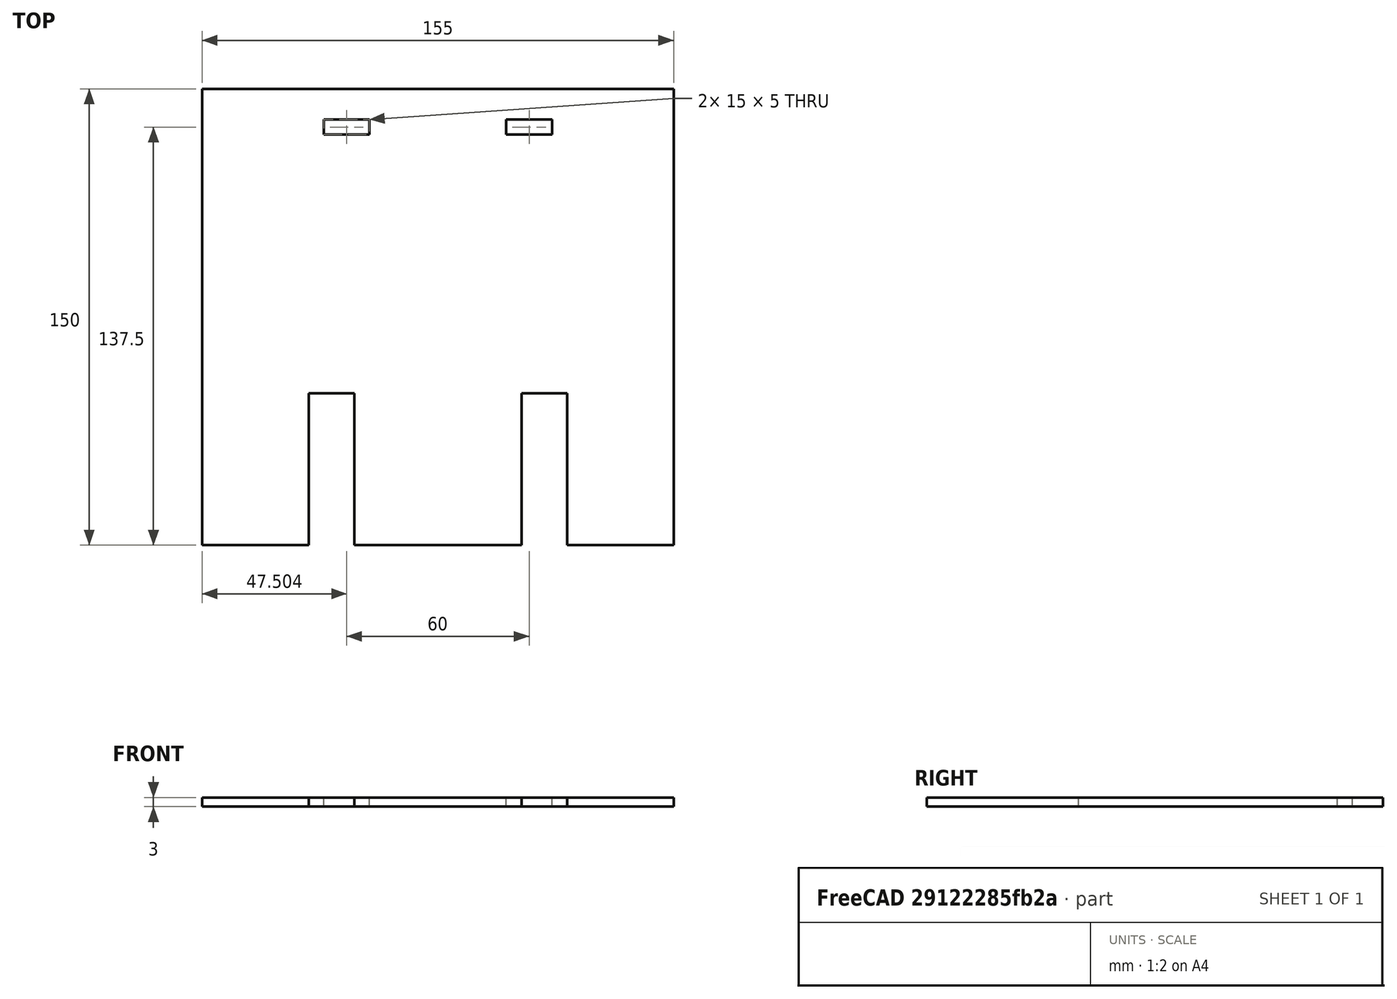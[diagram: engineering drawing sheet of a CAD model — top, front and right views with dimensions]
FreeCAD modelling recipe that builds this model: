
FCSTD DOCUMENT  (FreeCAD 0.16R6704 (Git))
Label: Platte
License: All rights reserved
LicenseURL: http://en.wikipedia.org/wiki/All_rights_reserved
objects: Sketcher::SketchObject×3, PartDesign::Pad×1
note: 5 computed .brp shape members not serialized (recipe doc carries the construction recipe); baked Part::Feature solids carry a one-line shape summary decoded from their .brp

FEATURE [Sketcher::SketchObject] Sketch
  sketch-geometry (24):
    g0: LineSegment StartX=-60.2556 StartY=82.8295 StartZ=0 EndX=94.7444 EndY=82.8295 EndZ=0
    g1: LineSegment StartX=94.7444 StartY=82.8295 StartZ=0 EndX=94.7444 EndY=-67.1705 EndZ=0
    g2: LineSegment StartX=-60.2556 StartY=-67.1705 StartZ=0 EndX=-60.2556 EndY=82.8295 EndZ=0
    g3: LineSegment StartX=-60.2556 StartY=-67.1705 StartZ=0 EndX=-25.2556 EndY=-67.1705 EndZ=0
    g4: LineSegment StartX=-25.2556 StartY=-67.1705 StartZ=0 EndX=-25.2556 EndY=-17.1705 EndZ=0
    g5: LineSegment StartX=-25.2556 StartY=-17.1705 StartZ=0 EndX=-10.2556 EndY=-17.1705 EndZ=0
    g6: LineSegment StartX=-10.2556 StartY=-17.1705 StartZ=0 EndX=-10.2556 EndY=-67.1705 EndZ=0
    g7: LineSegment StartX=-10.2556 StartY=-67.1705 StartZ=0 EndX=44.7444 EndY=-67.1705 EndZ=0
    g8: LineSegment StartX=44.7444 StartY=-67.1705 StartZ=0 EndX=44.7444 EndY=-17.1705 EndZ=0
    g9: LineSegment StartX=44.7444 StartY=-17.1705 StartZ=0 EndX=59.7444 EndY=-17.1705 EndZ=0
    g10: LineSegment StartX=59.7444 StartY=-17.1705 StartZ=0 EndX=59.7444 EndY=-67.1705 EndZ=0
    g11: LineSegment StartX=59.7444 StartY=-67.1705 StartZ=0 EndX=94.7444 EndY=-67.1705 EndZ=0
    g12: LineSegment StartX=-20.2556 StartY=72.8295 StartZ=0 EndX=-5.25563 EndY=72.8295 EndZ=0
    g13: LineSegment StartX=-5.25563 StartY=72.8295 StartZ=0 EndX=-5.25563 EndY=67.8295 EndZ=0
    g14: LineSegment StartX=-5.25563 StartY=67.8295 StartZ=0 EndX=-20.2556 EndY=67.8295 EndZ=0
    g15: LineSegment StartX=-20.2556 StartY=67.8295 StartZ=0 EndX=-20.2556 EndY=72.8295 EndZ=0
    g16: LineSegment StartX=39.7444 StartY=67.8295 StartZ=0 EndX=54.7444 EndY=67.8295 EndZ=0
    g17: LineSegment StartX=54.7444 StartY=67.8295 StartZ=0 EndX=54.7444 EndY=72.8295 EndZ=0
    g18: LineSegment StartX=54.7444 StartY=72.8295 StartZ=0 EndX=39.7444 EndY=72.8295 EndZ=0
    g19: LineSegment StartX=39.7444 StartY=72.8295 StartZ=0 EndX=39.7444 EndY=67.8295 EndZ=0
    g20: LineSegment [constr] StartX=-20.2556 StartY=72.8295 StartZ=0 EndX=-20.2556 EndY=82.8295 EndZ=0
    g21: LineSegment [constr] StartX=-20.2556 StartY=67.8295 StartZ=0 EndX=-60.2556 EndY=67.8295 EndZ=0
    g22: LineSegment [constr] StartX=54.7444 StartY=72.8295 StartZ=0 EndX=94.7444 EndY=72.8295 EndZ=0
    g23: LineSegment [constr] StartX=54.7444 StartY=72.8295 StartZ=0 EndX=54.7444 EndY=82.8295 EndZ=0
  constraints (70):
    c: Coincident(g0,g1)
    c: Coincident(g2,g0)
    c: Horizontal(g0)
    c: Vertical(g1)
    c: Vertical(g2)
    c: DistanceX(g0,g0) = 155
    c: DistanceY(g1,g1) = 150
    c: Coincident(g3,g2)
    c: Horizontal(g3)
    c: DistanceX(g3,g3) = 35
    c: Coincident(g4,g3)
    c: Vertical(g4)
    c: Coincident(g5,g4)
    c: Horizontal(g5)
    c: DistanceY(g4,g4) = 50
    c: DistanceX(g5,g5) = 15
    c: Coincident(g6,g5)
    c: Vertical(g6)
    c: DistanceY(g2,g2) = 150
    c: DistanceY(g6,g6) = 50
    c: Coincident(g7,g6)
    c: Horizontal(g7)
    c: DistanceX(g7,g7) = 55
    c: Coincident(g8,g7)
    c: Vertical(g8)
    c: Coincident(g9,g8)
    c: Horizontal(g9)
    c: Coincident(g10,g9)
    c: Vertical(g10)
    c: Coincident(g11,g10)
    c: Coincident(g11,g1)
    c: Horizontal(g11)
    c: DistanceX(g9,g9) = 15
    c: DistanceY(g10,g10) = 50
    c: Coincident(g12,g13)
    c: Coincident(g13,g14)
    c: Coincident(g14,g15)
    c: Coincident(g15,g12)
    c: Horizontal(g12)
    c: Horizontal(g14)
    c: Vertical(g13)
    c: Vertical(g15)
    c: Coincident(g16,g17)
    c: Coincident(g17,g18)
    c: Coincident(g18,g19)
    c: Coincident(g19,g16)
    c: Horizontal(g16)
    c: Horizontal(g18)
    c: Vertical(g17)
    c: Vertical(g19)
    c: Equal(g12,g16)
    c: Equal(g15,g19)
    c: Coincident(g20,g12)
    c: PointOnObject(g20,g0)
    c: Vertical(g20)
    c: Coincident(g21,g14)
    c: PointOnObject(g21,g2)
    c: Horizontal(g21)
    c: Coincident(g22,g17)
    c: PointOnObject(g22,g1)
    c: Horizontal(g22)
    c: DistanceX(g22,g22) = 40
    c: Coincident(g23,g17)
    c: PointOnObject(g23,g0)
    c: Vertical(g23)
    c: DistanceY(g23,g23) = 10
    c: DistanceX(g12,g12) = 15
    c: DistanceY(g15,g15) = 5
    c: DistanceX(g21,g21) = 40
    c: DistanceY(g20,g20) = 10
FEATURE [PartDesign::Pad] Pad
  Length = 3
  Length2 = 100
  Sketch = -> Sketch
  Type = 0
FEATURE [Sketcher::SketchObject] Sketch001
  Placement = pos=(0,0,3) rot=(0,0,1;0rad)
  Support = -> Pad [Face22]
FEATURE [Sketcher::SketchObject] Sketch002
  Placement = pos=(0,0,3) rot=(0,0,1;0rad)
  Support = -> Pad [Face22]
  sketch-geometry (4):
    g0: LineSegment [constr] StartX=-60.2556 StartY=82.8295 StartZ=0 EndX=-60.2556 EndY=-67.1705 EndZ=0
    g1: LineSegment [constr] StartX=-60.2556 StartY=-67.1705 StartZ=0 EndX=94.7444 EndY=-67.1705 EndZ=0
    g2: LineSegment [constr] StartX=94.7444 StartY=-67.1705 StartZ=0 EndX=94.7444 EndY=82.8295 EndZ=0
    g3: LineSegment [constr] StartX=94.7444 StartY=82.8295 StartZ=0 EndX=-60.2556 EndY=82.8295 EndZ=0
  constraints (12):
    c: Vertical(g0)
    c: Coincident(g1,g0)
    c: Horizontal(g1)
    c: Coincident(g2,g1)
    c: Vertical(g2)
    c: Coincident(g3,g2)
    c: Coincident(g3,g0)
    c: Horizontal(g3)
    c: DistanceX(g3,g3) = 155
    c: DistanceY(g2,g2) = 150
    c: DistanceY(g0,g0) = 150
    c: DistanceX(g1,g1) = 155
